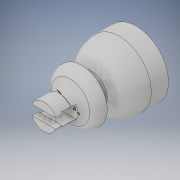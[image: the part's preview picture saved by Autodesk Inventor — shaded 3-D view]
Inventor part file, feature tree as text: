
AUTODESK INVENTOR PART (.ipt)
format: ipt  version: 2018 (Build 220112000, 112)  size: 208,896 bytes
history: native  units: mm
features: sketch x11, extrude x10, fillet x3
ambient origin geometry x8: Origin, YZ Plane, XZ Plane, XY Plane, X Axis, Y Axis, Z Axis, Center Point
bodies: Volumenkörper1 (feature_tree)
feature tree (24):
  extrude  "Extrusion1"  Depth=2.0mm TaperAngle=0.0deg
  fillet  "Rundung1"  Radius=2.0mm
  extrude  "Extrusion2"  Depth=1.5mm TaperAngle=0.0deg
  extrude  "Extrusion3"  Depth=10.0mm TaperAngle=0.0deg
  extrude  "Extrusion5"  Depth=2.0mm TaperAngle=0.0deg
  extrude  "Extrusion6"  Depth=2.0mm TaperAngle=0.0deg
  extrude  "Extrusion7"  Depth=1.1mm TaperAngle=0.0deg
  fillet  "Rundung2"  Radius=5.0mm
  sketch  "Skizze11"  dims[d23=4.0mm d24=4.0mm]
  extrude  "Extrusion8"  Depth=4.0mm
  extrude  "Extrusion9"  Depth=2.15mm TaperAngle=0.0deg
  extrude  "Extrusion10"  Depth=4.0mm TaperAngle=0.0deg
  extrude  "Extrusion11"  Depth=2.0mm
  fillet  "Rundung3"  [1 undecoded]
  sketch  "Skizze1"  dims[d0=8.0mm d1=2.0mm d2=0.0mm d3=2.0mm]
  sketch  "Skizze2"  dims[d4=5.0mm d5=1.5mm d6=0.0mm]
  sketch  "Skizze3"  dims[d7=10.0mm d8=5.0mm d9=0.0mm]
  sketch  "Skizze5"  dims[d13=10.0mm d14=2.0mm d15=0.0mm]
  sketch  "Skizze6"  dims[d16=8.5mm d17=2.0mm d18=0.0mm]
  sketch  "Skizze8"  dims[d19=1.6mm d20=1.1mm d21=0.0mm d22=5.0mm]
  sketch  "Skizze12"  dims[d25=2.85mm d26=0.0mm d27=2.15mm d28=0.0mm]
  sketch  "Skizze13"  dims[d29=4.0mm d30=1.0mm d31=0.0mm]
  sketch  "Skizze14"  dims[d32=1.0mm d33=0.0mm d34=2.0mm]
  sketch  "Skizze15"
note: 1 required parameter value undecoded (feature->parameter linkage not recoverable at this tier; creation-order binding heuristic only, values carry confidence <= 0.55)
